# Revit family: SP1012-2_Revit
name_source: partatom
category: Mechanical Equipment
revit_build: Autodesk Revit 2014 (Build: 20130215_1615(x64)
units: mm (PartAtom-declared; Revit-internal decimal feet)

## types (1)
- Standard
    Connector_11_Diameter = 0' - 0"
    Connector_12_Diameter = 0' - 0"
    Connector_13_Diameter = 0' - 0"
    Connector_14_Diameter = 0' - 0"
    Connector_15_Diameter = 0' - 0"
    Connector_16_Diameter = 0' - 0"
    Connector_17_Diameter = 0' - 0"
    Connector_18_Diameter = 0' - 0"
    Connector_19_Diameter = 0' - 0"
    Connector_1_Diameter = 0' - 0"
    Connector_2_Diameter = 0' - 0"
    Connector_3_Diameter = 0' - 0"
    Connector_4_Diameter = 0' - 0"
    Connector_5_Height = 0' - 0"
    Connector_5_Width = 0' - 0"
    Connector_6_Height = 0' - 0"
    Connector_6_Width = 0' - 0"
    Description = Gas Fired humidifier (2 modules)
    Design Status = 1
    Manufacturer = Neptronic
    Model = SKG3265, SKG3310, SKG3350, SKG3405
    Part Number = SP1012-2_Revit
    URL = www.neptronic.com
    d100 = 0' - 2 5/16"
    d102 = 0' - 2 5/16"
    d104 = 0' - 0 1/2"
    d106 = 0' - 0 1/2"
    d108 = 0' - 0 1/2"
    d110 = 0' - 0 1/2"
    d114 = 0' - 0 1/2"
    d116 = 0' - 0 1/2"
    d118 = 0' - 0 1/2"
    d120 = 0' - 0 1/2"
    d122 = 0' - 1 9/16"
    d124 = 0' - 0 1/2"
    d126 = 0' - 0 1/2"
    d128 = 0' - 0 1/2"
    d130 = 0' - 0 1/2"
    d132 = 0' - 0 1/2"
    d134 = 0' - 0 1/2"
    d136 = 0' - 0 1/2"
    d138 = 0' - 0 1/2"
    d140 = 0' - 0 1/2"
    d142 = 0' - 0 1/2"
    d144 = 0' - 0 1/2"
    d146 = 0' - 2 1/32"
    d148 = 0' - 2 1/32"
    d150 = 0' - 2 1/32"
    d152 = 0' - 2 1/32"
    d154 = 0' - 2 1/32"
    d156 = 0' - 2 1/32"
    d158 = 0' - 2 1/32"
    d160 = 3' - 8 15/16"
    d162 = 3' - 8 15/16"
    d164 = 0' - 5"
    d166 = 0' - 2 1/8"
    d168 = 0' - 5"
    d170 = 4' - 4"
    d172 = 3' - 9 3/16"
    d174 = 0' - 5 1/4"
    d177 = 0' - 0"
    d98 = 0' - 3 23/32"

## geometry (parser evidence)
native form markers: Sweep x1
no freeform markers — native parametric forms only
